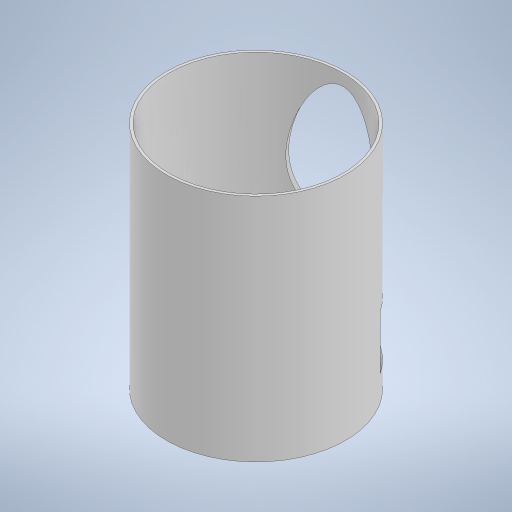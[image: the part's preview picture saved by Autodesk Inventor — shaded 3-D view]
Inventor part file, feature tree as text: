
AUTODESK INVENTOR PART (.ipt)
format: ipt  version: 2024.3 (Build 283343000, 343)  size: 243,200 bytes
history: native  units: mm
features: sketch x4, extrude x3, plane x1
ambient origin geometry x8: Origin, YZ Plane, XZ Plane, XY Plane, X Axis, Y Axis, Z Axis, Center Point
bodies: Solid1 (feature_tree)
feature tree (8):
  extrude  "Extrusion1"  Depth=140.0mm
  extrude  "Extrusion2"  Depth=42.0mm
  sketch  "Sketch3"  dims[d5=116.0mm d6=20.0mm]
  plane  "Work Plane1"
  extrude  "Extrusion3"  Depth=20.0mm
  sketch  "Sketch1"  dims[d0=2.0mm d1=140.0mm]
  sketch  "Sketch2"  dims[d2=180.0mm d3=0.0mm d4=42.0mm]
  sketch  "Sketch4"  dims[d7=58.0mm d8=0.0mm d9=0.0mm d10=135.0deg d11=70.0mm d12=110.0mm d13=0.0mm d14=0.0mm d15=40.0mm]
